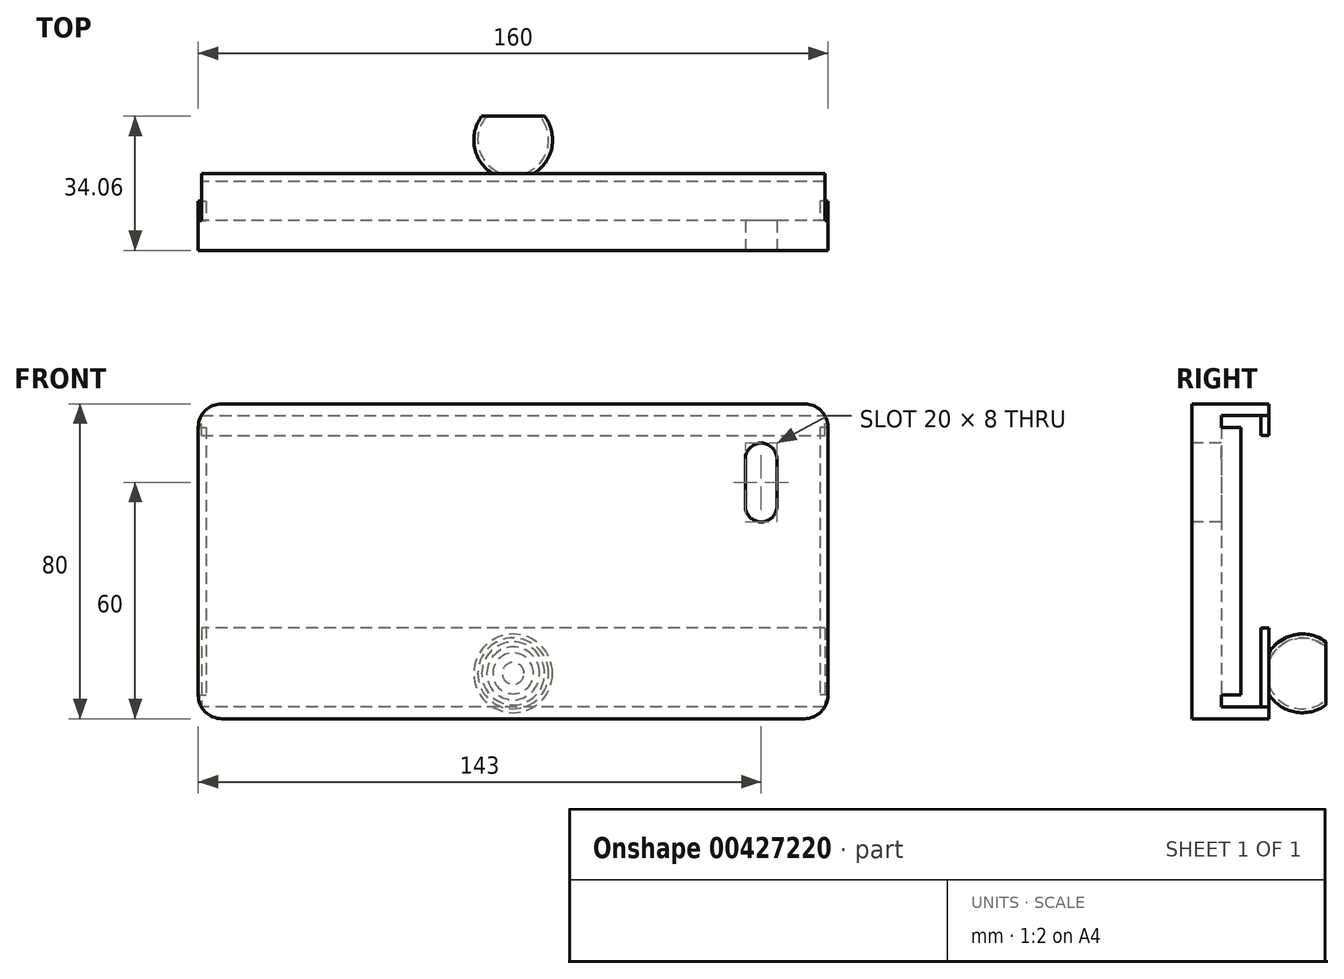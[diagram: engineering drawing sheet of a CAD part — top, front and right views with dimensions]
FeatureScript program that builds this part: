
annotation { "Feature Type Name" : "Feature", "Feature Type Description" : "" }
export const myFeature = defineFeature(function(context is Context, id is Id, definition is map)
    precondition{}
    {
        {
            var Q0;
            Q0=qCreatedBy(makeId("Front.planeOp"),FACE);
            var sketch = newSketch(context, id + "F0", { "sketchPlane" : qUnion([Q0])});
            skLineSegment(sketch, "E0.bottom", {"start": v(-80, 40) * mm, "end": v(80, 40) * mm});
            skLineSegment(sketch, "E0.top", {"start": v(-80, -40) * mm, "end": v(80, -40) * mm});
            skLineSegment(sketch, "E0.left", {"start": v(-80, 40) * mm, "end": v(-80, -40) * mm});
            skLineSegment(sketch, "E0.right", {"start": v(80, 40) * mm, "end": v(80, -40) * mm});
            skPoint(sketch, "E0.middle", {"position": v(0, 0) * mm});
            skSolve(sketch);
        }
        {
            var Q0;
            Q0 = qSketchRegion(id + "F0", true);
            extrude(context, id + "F1", {"entities" : qUnion([Q0]), "depth" : 7.5 * mm});
        }
        {
            var Q0;
            Q0=makeQuery(id+"F1.opExtrude","CAP_FACE",FACE,{"disambiguationData":[OSD([sQuery(id+"F0.wireOp",EDGE,"E0.bottom"),sQuery(id+"F0.wireOp",EDGE,"E0.top"),sQuery(id+"F0.wireOp",EDGE,"E0.left"),sQuery(id+"F0.wireOp",EDGE,"E0.right")])],"isStart":false});
            var sketch = newSketch(context, id + "F2", { "sketchPlane" : qUnion([Q0])});
            skCircle(sketch, "E1", {"center": v(63, 26) * mm, "radius": 4 * mm});
            skLineSegment(sketch, "E2.bottom", {"start": v(59, 26) * mm, "end": v(67, 26) * mm});
            skLineSegment(sketch, "E2.top", {"start": v(59, 14) * mm, "end": v(67, 14) * mm});
            skLineSegment(sketch, "E2.left", {"start": v(59, 26) * mm, "end": v(59, 14) * mm});
            skLineSegment(sketch, "E2.right", {"start": v(67, 26) * mm, "end": v(67, 14) * mm});
            skCircle(sketch, "E3", {"center": v(63, 14) * mm, "radius": 4 * mm});
            skSolve(sketch);
        }
        {
            var Q0;
            Q0 = qSketchRegion(id + "F2", true);
            extrude(context, id + "F3", {"entities" : qUnion([Q0]), "operationType" : NewBodyOperationType.REMOVE, "oppositeDirection" : true, "depth" : 11.3 * mm});
        }
        {
            var Q0;
            Q0=makeQuery(id+"F1.opExtrude","SWEPT_EDGE",EDGE,{"disambiguationData":[OSD([sQuery(id+"F0.wireOp",EDGE,"E0.bottom"),sQuery(id+"F0.wireOp",EDGE,"E0.left")])]});
            var Q1;
            Q1=makeQuery(id+"F1.opExtrude","SWEPT_EDGE",EDGE,{"disambiguationData":[OSD([sQuery(id+"F0.wireOp",EDGE,"E0.bottom"),sQuery(id+"F0.wireOp",EDGE,"E0.right")])]});
            var Q2;
            Q2=makeQuery(id+"F1.opExtrude","SWEPT_EDGE",EDGE,{"disambiguationData":[OSD([sQuery(id+"F0.wireOp",EDGE,"E0.top"),sQuery(id+"F0.wireOp",EDGE,"E0.right")])]});
            var Q3;
            Q3=makeQuery(id+"F1.opExtrude","SWEPT_EDGE",EDGE,{"disambiguationData":[OSD([sQuery(id+"F0.wireOp",EDGE,"E0.top"),sQuery(id+"F0.wireOp",EDGE,"E0.left")])]});
            fillet(context, id + "F4", {"entities" : qUnion([Q0, Q1, Q2, Q3]), "radius" : 6 * mm, "tangentPropagation" : true, "allowEdgeOverflow" : false});
        }
        {
            var Q0;
            Q0=makeQuery(id+"F1.opExtrude","CAP_FACE",FACE,{"disambiguationData":[OSD([sQuery(id+"F0.wireOp",EDGE,"E0.bottom"),sQuery(id+"F0.wireOp",EDGE,"E0.top"),sQuery(id+"F0.wireOp",EDGE,"E0.left"),sQuery(id+"F0.wireOp",EDGE,"E0.right")])],"isStart":true});
            var sketch = newSketch(context, id + "F5", { "sketchPlane" : qUnion([Q0])});
            skLineSegment(sketch, "E4", {"start": v(-74, 40) * mm, "end": v(74, 40) * mm});
            skLineSegment(sketch, "E5", {"start": v(59.06, 37) * mm, "end": v(-79.2, 37) * mm});
            skLineSegment(sketch, "E6", {"start": v(-79.2, 37) * mm, "end": v(79.2, 37) * mm});
            skArc(sketch, "E7", {"start": v(79.2, 37) * mm, "mid": v(77, 39.2) * mm, "end": v(74, 40) * mm});
            skArc(sketch, "E8", {"start": v(-74, 40) * mm, "mid": v(-77, 39.2) * mm, "end": v(-79.2, 37) * mm});
            skSolve(sketch);
        }
        {
            var Q0;
            Q0 = qSketchRegion(id + "F5", true);
            extrude(context, id + "F6", {"entities" : qUnion([Q0]), "operationType" : NewBodyOperationType.ADD, "depth" : 12 * mm});
        }
        {
            var Q0;
            Q0=makeQuery(id+"F6.opExtrude","SWEPT_FACE",FACE,{"disambiguationData":[OSD([sQuery(id+"F5.wireOp",EDGE,"E6")])]});
            var sketch = newSketch(context, id + "F7", { "sketchPlane" : qUnion([Q0])});
            skLineSegment(sketch, "E9.bottom", {"start": v(-79.2, -12) * mm, "end": v(79.2, -12) * mm});
            skLineSegment(sketch, "E9.top", {"start": v(-79.2, -10) * mm, "end": v(79.2, -10) * mm});
            skLineSegment(sketch, "E9.left", {"start": v(79.2, -12) * mm, "end": v(79.2, -10) * mm});
            skLineSegment(sketch, "E9.right", {"start": v(-79.2, -12) * mm, "end": v(-79.2, -10) * mm});
            skSolve(sketch);
        }
        {
            var Q0;
            Q0 = qSketchRegion(id + "F7", true);
            extrude(context, id + "F8", {"entities" : qUnion([Q0]), "operationType" : NewBodyOperationType.ADD, "depth" : 5 * mm});
        }
        {
            var Q0;
            Q0=makeQuery(id+"F1.opExtrude","CAP_FACE",FACE,{"disambiguationData":[OSD([sQuery(id+"F0.wireOp",EDGE,"E0.bottom"),sQuery(id+"F0.wireOp",EDGE,"E0.top"),sQuery(id+"F0.wireOp",EDGE,"E0.left"),sQuery(id+"F0.wireOp",EDGE,"E0.right")])],"isStart":true});
            var sketch = newSketch(context, id + "F9", { "sketchPlane" : qUnion([Q0])});
            skLineSegment(sketch, "E10", {"start": v(74, -40) * mm, "end": v(-74, -40) * mm});
            skLineSegment(sketch, "E11", {"start": v(-74, -37) * mm, "end": v(-79.2, -37) * mm});
            skLineSegment(sketch, "E12", {"start": v(-79.2, -37) * mm, "end": v(79.2, -37) * mm});
            skArc(sketch, "E13", {"start": v(-79.2, -37) * mm, "mid": v(-77, -39.2) * mm, "end": v(-74, -40) * mm});
            skArc(sketch, "E14", {"start": v(74, -40) * mm, "mid": v(77, -39.2) * mm, "end": v(79.2, -37) * mm});
            skSolve(sketch);
        }
        {
            var Q0;
            Q0 = qSketchRegion(id + "F9", true);
            extrude(context, id + "F10", {"entities" : qUnion([Q0]), "operationType" : NewBodyOperationType.ADD, "depth" : 12 * mm});
        }
        {
            var Q0;
            Q0=makeQuery(id+"F10.opExtrude","SWEPT_FACE",FACE,{"disambiguationData":[OSD([sQuery(id+"F9.wireOp",EDGE,"E12")])]});
            var sketch = newSketch(context, id + "F11", { "sketchPlane" : qUnion([Q0])});
            skSolve(sketch);
        }
        {
            var Q0;
            {var subQ0=sQuery(id+"F9.wireOp",EDGE,"E12");Q0=makeQuery(id+"F11.imprint","IMPRINT",FACE,{"disambiguationData":[TD([[makeQuery(id+"F11.imprint","IMPRINT",EDGE,{"derivedFrom":makeQuery(id+"F10.opExtrude","CAP_EDGE",EDGE,{"disambiguationData":[OSD([subQ0])],"isStart":false})}),1.0]])]});}
            var sketch = newSketch(context, id + "F12", { "sketchPlane" : qUnion([Q0])});
            skLineSegment(sketch, "E15.bottom", {"start": v(79.2, 12) * mm, "end": v(-79.2, 12) * mm});
            skLineSegment(sketch, "E15.top", {"start": v(79.2, 10) * mm, "end": v(-79.2, 10) * mm});
            skLineSegment(sketch, "E15.left", {"start": v(79.2, 12) * mm, "end": v(79.2, 10) * mm});
            skLineSegment(sketch, "E15.right", {"start": v(-79.2, 12) * mm, "end": v(-79.2, 10) * mm});
            skSolve(sketch);
        }
        {
            var Q0;
            Q0 = qSketchRegion(id + "F12", true);
            extrude(context, id + "F13", {"entities" : qUnion([Q0]), "operationType" : NewBodyOperationType.ADD, "depth" : 20 * mm});
        }
        {
            var Q0;
            Q0=makeQuery(id+"F1.opExtrude","CAP_FACE",FACE,{"disambiguationData":[OSD([sQuery(id+"F0.wireOp",EDGE,"E0.bottom"),sQuery(id+"F0.wireOp",EDGE,"E0.top"),sQuery(id+"F0.wireOp",EDGE,"E0.left"),sQuery(id+"F0.wireOp",EDGE,"E0.right")])],"isStart":true});
            var sketch = newSketch(context, id + "F14", { "sketchPlane" : qUnion([Q0])});
            skLineSegment(sketch, "E16.bottom", {"start": v(80, 34) * mm, "end": v(78, 34) * mm});
            skLineSegment(sketch, "E16.top", {"start": v(80, -34) * mm, "end": v(78, -34) * mm});
            skLineSegment(sketch, "E16.left", {"start": v(80, 34) * mm, "end": v(80, -34) * mm});
            skLineSegment(sketch, "E16.right", {"start": v(78, 34) * mm, "end": v(78, -34) * mm});
            skLineSegment(sketch, "E17.bottom", {"start": v(-80, 34) * mm, "end": v(-78, 34) * mm});
            skLineSegment(sketch, "E17.top", {"start": v(-80, -34) * mm, "end": v(-78, -34) * mm});
            skLineSegment(sketch, "E17.left", {"start": v(-80, 34) * mm, "end": v(-80, -34) * mm});
            skLineSegment(sketch, "E17.right", {"start": v(-78, 34) * mm, "end": v(-78, -34) * mm});
            skSolve(sketch);
        }
        {
            var Q0;
            Q0 = qSketchRegion(id + "F14", true);
            extrude(context, id + "F15", {"entities" : qUnion([Q0]), "operationType" : NewBodyOperationType.ADD, "depth" : 5 * mm});
        }
        {
            var Q0;
            Q0=makeQuery(id+"F13.boolean.opBoolean","MERGE",FACE,{"derivedFrom":[makeQuery(id+"F10.opExtrude","CAP_FACE",FACE,{"disambiguationData":[OSD([sQuery(id+"F9.wireOp",EDGE,"E10"),sQuery(id+"F9.wireOp",EDGE,"E12"),sQuery(id+"F9.wireOp",EDGE,"E13"),sQuery(id+"F9.wireOp",EDGE,"E14")])],"isStart":false}),makeQuery(id+"F13.opExtrude","SWEPT_FACE",FACE,{"disambiguationData":[OSD([sQuery(id+"F12.wireOp",EDGE,"E15.bottom")])]})]});
            var sketch = newSketch(context, id + "F16", { "sketchPlane" : qUnion([Q0])});
            skLineSegment(sketch, "E18.bottom", {"start": v(0, -28.5) * mm, "end": v(-10, -28.5) * mm});
            skLineSegment(sketch, "E18.top", {"start": v(0, -37.24) * mm, "end": v(-10, -37.24) * mm});
            skLineSegment(sketch, "E18.left", {"start": v(0, -28.5) * mm, "end": v(0, -37.24) * mm});
            skLineSegment(sketch, "E18.right", {"start": v(-10, -28.5) * mm, "end": v(-10, -37.24) * mm});
            skSolve(sketch);
        }
        {
            var Q0;
            Q0 = qSketchRegion(id + "F16", true);
            extrude(context, id + "F17", {"entities" : qUnion([Q0]), "operationType" : NewBodyOperationType.ADD, "depth" : 40 * mm});
        }
        {
            var Q0;
            Q0=makeQuery(id+"F17.opExtrude","SWEPT_FACE",FACE,{"disambiguationData":[OSD([sQuery(id+"F16.wireOp",EDGE,"E18.bottom")])]});
            var sketch = newSketch(context, id + "F18", { "sketchPlane" : qUnion([Q0])});
            skArc(sketch, "E19", {"start": v(10, 20.56) * mm, "mid": v(8.7, 15.65) * mm, "end": v(5.17, 12) * mm});
            skArc(sketch, "E20", {"start": v(10, 20.56) * mm, "mid": v(-4.91, 29.27) * mm, "end": v(-5.17, 12) * mm});
            skLineSegment(sketch, "E21", {"start": v(-5.17, 12) * mm, "end": v(5.17, 12) * mm});
            skArc(sketch, "E22", {"start": v(9, 20.56) * mm, "mid": v(-5.29, 27.84) * mm, "end": v(-2.78, 12) * mm});
            skArc(sketch, "E23", {"start": v(9, 20.56) * mm, "mid": v(7.28, 15.27) * mm, "end": v(2.78, 12) * mm});
            skLineSegment(sketch, "E24", {"start": v(10, 26.56) * mm, "end": v(-14.04, 26.56) * mm});
            skArc(sketch, "E25", {"start": v(2.78, 12) * mm, "mid": v(0, 11.56) * mm, "end": v(-2.78, 12) * mm});
            skSolve(sketch);
        }
        {
            var Q0;
            {var subQ0=sQuery(id+"F18.wireOp",EDGE,"E21");var subQ1=sQuery(id+"F18.wireOp",EDGE,"E20");var subQ2=makeQuery(id+"F18.imprint","INTERSECT",VERTEX,{"derivedFrom":[subQ1,subQ0]});Q0=makeQuery(id+"F18.imprint","IMPRINT",FACE,{"disambiguationData":[TD([[makeQuery(id+"F18.imprint","IMPRINT",EDGE,{"disambiguationData":[TD([[subQ2,1.0]])],"derivedFrom":subQ1}),1.0]])]});}
            var Q1;
            Q1=makeQuery(id+"F17.opExtrude","SWEPT_EDGE",EDGE,{"disambiguationData":[OSD([sQuery(id+"F16.wireOp",EDGE,"E18.bottom"),sQuery(id+"F16.wireOp",EDGE,"E18.left")])]});
            revolve(context, id + "F19", {"operationType" : NewBodyOperationType.ADD, "entities" : qUnion([Q0]), "axis" : qUnion([Q1]), "revolveType" : RevolveType.FULL});
        }
        {
            var Q0;
            {var subQ0=sQuery(id+"F16.wireOp",EDGE,"E18.left");var subQ1=sQuery(id+"F16.wireOp",EDGE,"E18.right");var subQ2=sQuery(id+"F16.wireOp",EDGE,"E18.bottom");var subQ3=makeQuery(id+"F17.opExtrude","SWEPT_FACE",FACE,{"disambiguationData":[OSD([subQ2])]});Q0=makeQuery(id+"F19.boolean.opBoolean","SPLIT",FACE,{"disambiguationData":[TD([subQ3,makeQuery(id+"F17.opExtrude","CAP_FACE",FACE,{"disambiguationData":[OSD([subQ2,sQuery(id+"F16.wireOp",EDGE,"E18.top"),subQ0,subQ1])],"isStart":false}),makeQuery(id+"F17.opExtrude","SWEPT_FACE",FACE,{"disambiguationData":[OSD([subQ0])]}),makeQuery(id+"F17.opExtrude","SWEPT_FACE",FACE,{"disambiguationData":[OSD([subQ1])]}),makeQuery(id+"F19.opRevolve","SWEPT_FACE",FACE,{"disambiguationData":[OSD([sQuery(id+"F18.wireOp",EDGE,"E20")])]})])],"derivedFrom":subQ3});}
            var Q1;
            {var subQ0=sQuery(id+"F16.wireOp",EDGE,"E18.bottom");var subQ1=sQuery(id+"F16.wireOp",EDGE,"E18.left");Q1=makeQuery(id+"F19.boolean.opBoolean","SPLIT",EDGE,{"disambiguationData":[TD([makeQuery(id+"F19.opRevolve","SWEPT_FACE",FACE,{"disambiguationData":[OSD([sQuery(id+"F18.wireOp",EDGE,"E20")])]})])],"derivedFrom":makeQuery(id+"F17.opExtrude","SWEPT_EDGE",EDGE,{"disambiguationData":[OSD([subQ0,subQ1])]})});}
            revolve(context, id + "F20", {"operationType" : NewBodyOperationType.REMOVE, "entities" : qUnion([Q0]), "axis" : qUnion([Q1]), "revolveType" : RevolveType.FULL, "oppositeDirection" : true});
        }
        {
            var Q0;
            Q0=makeQuery(id+"F17.opExtrude","CAP_FACE",FACE,{"disambiguationData":[OSD([sQuery(id+"F16.wireOp",EDGE,"E18.bottom"),sQuery(id+"F16.wireOp",EDGE,"E18.top"),sQuery(id+"F16.wireOp",EDGE,"E18.left"),sQuery(id+"F16.wireOp",EDGE,"E18.right")])],"isStart":false});
            extrude(context, id + "F21", {"entities" : qUnion([Q0]), "operationType" : NewBodyOperationType.REMOVE, "oppositeDirection" : true, "depth" : 40 * mm});
        }
        {
            var Q0;
            {var subQ0=makeQuery(id+"F17.opExtrude","SWEPT_FACE",FACE,{"disambiguationData":[OSD([sQuery(id+"F16.wireOp",EDGE,"E18.bottom")])]});Q0=makeQuery(id+"F19.boolean.opBoolean","SPLIT",FACE,{"disambiguationData":[TD([makeQuery(id+"F13.opExtrude","SWEPT_FACE",FACE,{"disambiguationData":[OSD([sQuery(id+"F12.wireOp",EDGE,"E15.bottom")])]})])],"derivedFrom":subQ0});}
            var Q1;
            Q1=makeQuery(id+"F21.boolean.opBoolean","COPY",FACE,{"derivedFrom":makeQuery(id+"F21.opExtrude","SWEPT_FACE",FACE,{"disambiguationData":[OSD([sQuery(id+"F16.wireOp",EDGE,"E18.bottom"),sQuery(id+"F16.wireOp",EDGE,"E18.right")])]})});
            revolve(context, id + "F22", {"operationType" : NewBodyOperationType.REMOVE, "entities" : qUnion([Q0]), "axis" : qUnion([Q1]), "revolveType" : RevolveType.FULL});
        }
    });
